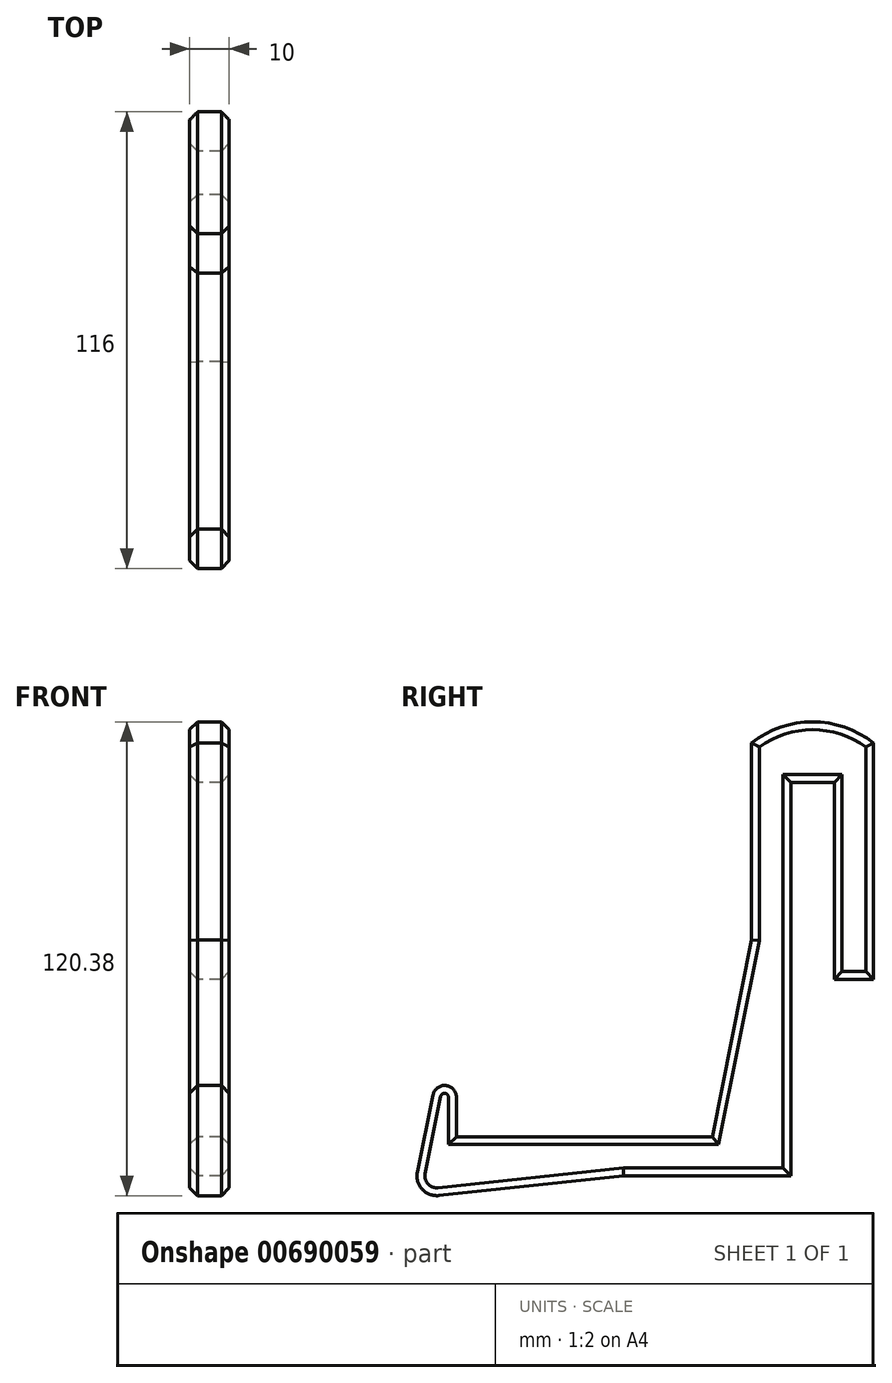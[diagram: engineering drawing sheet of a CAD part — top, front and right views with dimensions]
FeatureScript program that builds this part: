
annotation { "Feature Type Name" : "Feature", "Feature Type Description" : "" }
export const myFeature = defineFeature(function(context is Context, id is Id, definition is map)
    precondition{}
    {
        {
            var Q0;
            Q0=qCreatedBy(makeId("Right.planeOp"),FACE);
            var sketch = newSketch(context, id + "F0", { "sketchPlane" : qUnion([Q0])});
            skLineSegment(sketch, "E0", {"start": v(0, 0) * mm, "end": v(0, 100) * mm});
            skLineSegment(sketch, "E1", {"start": v(0, 100) * mm, "end": v(11, 100) * mm});
            skLineSegment(sketch, "E2", {"start": v(11, 100) * mm, "end": v(11, 50) * mm});
            skLineSegment(sketch, "E3", {"start": v(11, 50) * mm, "end": v(21, 50) * mm});
            skLineSegment(sketch, "E4", {"start": v(21, 50) * mm, "end": v(21, 110) * mm});
            skLineSegment(sketch, "E5", {"start": v(21, 110) * mm, "end": v(-10, 110) * mm, "construction": true});
            skLineSegment(sketch, "E6", {"start": v(-10, 110) * mm, "end": v(-10, 60) * mm});
            skLineSegment(sketch, "E7", {"start": v(-20, 10) * mm, "end": v(-85, 10) * mm});
            skLineSegment(sketch, "E8", {"start": v(-42.5, 0) * mm, "end": v(0, 0) * mm});
            skLineSegment(sketch, "E9", {"start": v(-85, 10) * mm, "end": v(-85, 20) * mm});
            skArc(sketch, "E10", {"start": v(-85, 20) * mm, "mid": v(-87.7, 22.99) * mm, "end": v(-90.94, 20.6) * mm});
            skArc(sketch, "E11", {"start": v(-89.47, -4.97) * mm, "mid": v(-93.7, -3.37) * mm, "end": v(-94.9, 1) * mm});
            skLineSegment(sketch, "E12", {"start": v(-90.94, 20.6) * mm, "end": v(-94.9, 1) * mm});
            skLineSegment(sketch, "E13", {"start": v(-89.47, -4.97) * mm, "end": v(-42.5, 0) * mm});
            skPoint(sketch, "E14.orphan", {"position": v(-85, 0) * mm});
            skLineSegment(sketch, "E15", {"start": v(-10, 60) * mm, "end": v(-20, 10) * mm});
            skPoint(sketch, "E16.orphan", {"position": v(-10, 10) * mm});
            skArc(sketch, "E17", {"start": v(21, 110) * mm, "mid": v(5.5, 115.38) * mm, "end": v(-10, 110) * mm});
            skSolve(sketch);
        }
        {
            var Q0;
            Q0=makeQuery(id+"F0.imprint","IMPRINT",FACE,{"disambiguationData":[TD([[makeQuery(id+"F0.imprint","IMPRINT",EDGE,{"derivedFrom":sQuery(id+"F0.wireOp",EDGE,"E0")}),1.0]])]});
            extrude(context, id + "F1", {"entities" : qUnion([Q0]), "depth" : 10 * mm, "offsetDistance" : 25 * mm});
        }
        {
            var Q0;
            Q0=makeQuery(id+"F1.opExtrude","CAP_FACE",FACE,{"disambiguationData":[OSD([sQuery(id+"F0.wireOp",EDGE,"E0"),sQuery(id+"F0.wireOp",EDGE,"E1"),sQuery(id+"F0.wireOp",EDGE,"E2"),sQuery(id+"F0.wireOp",EDGE,"E3"),sQuery(id+"F0.wireOp",EDGE,"E4"),sQuery(id+"F0.wireOp",EDGE,"E6"),sQuery(id+"F0.wireOp",EDGE,"E7"),sQuery(id+"F0.wireOp",EDGE,"E8"),sQuery(id+"F0.wireOp",EDGE,"E9"),sQuery(id+"F0.wireOp",EDGE,"E10"),sQuery(id+"F0.wireOp",EDGE,"E11"),sQuery(id+"F0.wireOp",EDGE,"E12"),sQuery(id+"F0.wireOp",EDGE,"E13"),sQuery(id+"F0.wireOp",EDGE,"E15"),sQuery(id+"F0.wireOp",EDGE,"E17")])],"isStart":true});
            var Q1;
            Q1=makeQuery(id+"F1.opExtrude","CAP_FACE",FACE,{"disambiguationData":[OSD([sQuery(id+"F0.wireOp",EDGE,"E0"),sQuery(id+"F0.wireOp",EDGE,"E1"),sQuery(id+"F0.wireOp",EDGE,"E2"),sQuery(id+"F0.wireOp",EDGE,"E3"),sQuery(id+"F0.wireOp",EDGE,"E4"),sQuery(id+"F0.wireOp",EDGE,"E6"),sQuery(id+"F0.wireOp",EDGE,"E7"),sQuery(id+"F0.wireOp",EDGE,"E8"),sQuery(id+"F0.wireOp",EDGE,"E9"),sQuery(id+"F0.wireOp",EDGE,"E10"),sQuery(id+"F0.wireOp",EDGE,"E11"),sQuery(id+"F0.wireOp",EDGE,"E12"),sQuery(id+"F0.wireOp",EDGE,"E13"),sQuery(id+"F0.wireOp",EDGE,"E15"),sQuery(id+"F0.wireOp",EDGE,"E17")])],"isStart":false});
            chamfer(context, id + "F2", {"entities" : qUnion([Q0, Q1]), "width" : 2 * mm, "tangentPropagation" : true});
        }
    });
